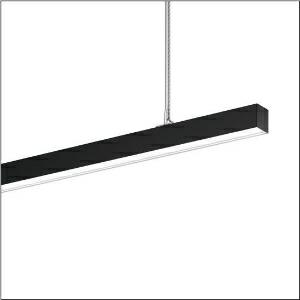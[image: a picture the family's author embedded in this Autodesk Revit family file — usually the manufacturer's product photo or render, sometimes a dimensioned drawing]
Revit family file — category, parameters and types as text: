
# Revit family: silica_r__21_51mx30tat4b_500a
name_source: partatom
category: Lighting Fixtures
units: mm (PartAtom-declared; Revit-internal decimal feet)

## family parameters
Cut with Voids When Loaded = No
Host = Face
Light Source = No
Part Type = Normal
Room Calculation Point = No
Round Connector Dimension = Use Diameter
Shared = No

## types (1)
- --- (1 x LED, 4120 lm, 33.8 W, 6500K)
    Apparent Load = 34 VA
    CIE Flux Codes = 47 79 96 58 100
    Color Rendering = 80
    Color Temperature = 6500K
    Default Elevation = 1800 mm
    Description = Silica® 21, office luminaire, primary optical cover: cover, of PMMA, opal, light emission: direct/indirect distribution, primary light characteristic: symmetric, installation type: suspended mounting, LED, rated luminous flux: 4.120lm, luminous efficacy: 116lm/W, light colour: 8tw, colour temperature: 2700..6500K, control gear: ECG DALI, with terminal, 3+2-pole, max. 2.5mm², mains connection: 220..240V, AC, 50/60Hz, rated input power: 35.5W, luminaire housing, of aluminium, jet black (RAL 9005), length: 1.204mm, width: 53mm, height: 53mm, protection rating (complete): IP20, insulation class (complete): insulation class I (protective earthing), certification: CE, permissible operating ambient temperature: 0..+35°C, standard: EN 50419, packaging unit: 1 piece
    Height = 53 mm
    Lamp = 1 x LED
    Lamp Light Flux = 4120 lm
    Lamp Power = 33.8 W
    Lamp count = 1
    Length = 1204 mm
    Luminous efficacy = 122 lm/W
    Manufacturer = Siteco
    ModVariant = No
    Model = 51MX30TAT4B
    Mounting Place = Ceiling
    Mounting Type = Pendant
    Number of Poles = 1
    OnlyDefault = Yes
    Power Factor = 1
    Product Name = Silica® 21
    Product group = office luminaire | ceiling pendant
    ProductGroupID = 905
    Protection Class = Protection class I
    Protection Degree = IP 20
    RLX_Detail_Level = 1
    RlxData = <blob elided: 22869 chars, md5=2cd4d323>
    Socket = socket
    Standby Power = 0 W
    System Light Flux = 4120 lm
    System Power = 34 W
    Type Comments = individual setting
    Type Image = l_1251735.jpg
    URL = http://relux.com
    VarID = @adj_045729
    Voltage = 0 V
    Weight = 0.00 kg
    Width = 53 mm

## geometry (parser evidence)
native form markers: Blend x4, Sweep x13
no freeform markers — native parametric forms only
